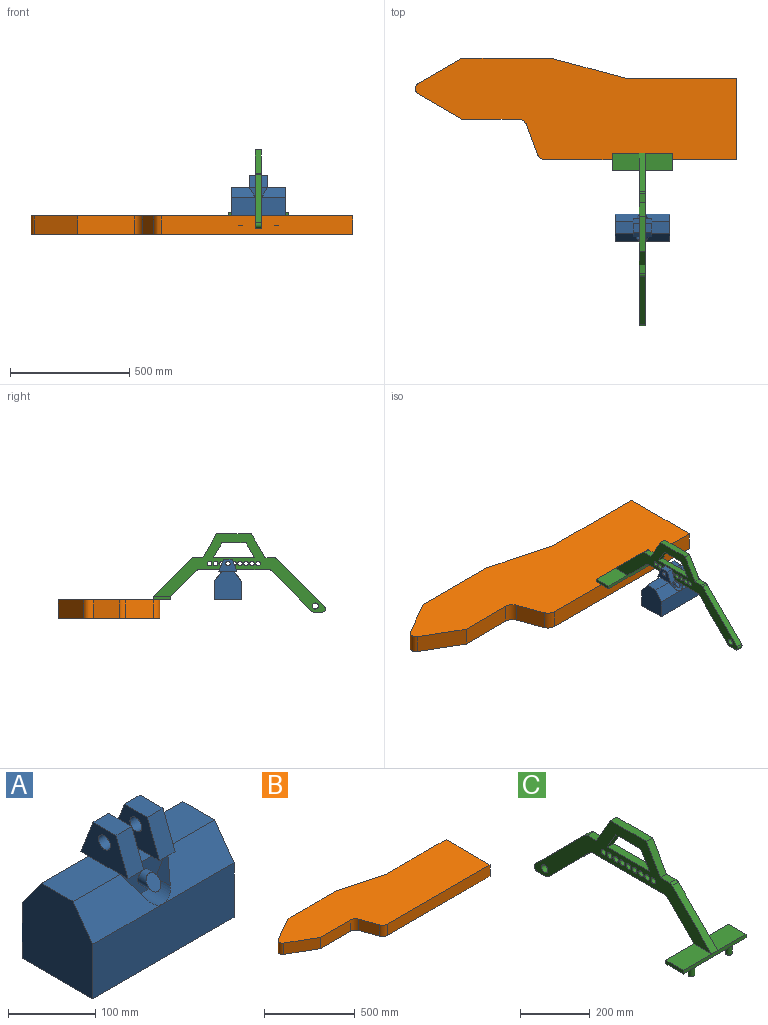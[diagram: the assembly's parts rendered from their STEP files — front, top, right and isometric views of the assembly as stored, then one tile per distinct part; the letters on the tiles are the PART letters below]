
ASSEMBLY  parts=3 mates=3
PART A: 40 faces, bbox 228.6x114.3x171.5 mm
  f0: plane 114.3x44.45mm, normal (0,0.81,0.58), area 4882.5mm2, adj f5,f6,f13,f35,f36
  f1: plane 114.3x44.45mm, normal (0,0.81,0.58), area 4882.5mm2, adj f4,f8,f13,f34,f35
  f2: plane 114.3x44.45mm, normal (0,-0.81,0.58), area 4882.5mm2, adj f4,f8,f14,f28,f31
  f3: plane 114.3x44.45mm, normal (0,-0.81,0.58), area 4882.5mm2, adj f5,f6,f14,f29,f31
  f4: plane 120.65x114.3mm, normal (1,0,0), area 12379mm2, adj f1,f2,f8,f13,f14,f15
  f5: plane 120.65x114.3mm, normal (-1,0,0), area 12379mm2, adj f0,f3,f6,f13,f14,f15
  f6: plane 76.2x50.8mm, normal (0,0,1), area 3871mm2, adj f0,f3,f5,f20
  f7: plane 50.8x25.4mm, normal (0,0,1), area 1290.3mm2, adj f22,f23,f32,f38
  f8: plane 76.2x50.8mm, normal (0,0,1), area 3871mm2, adj f1,f2,f4,f21
  f9: plane 37.2x25.4mm, normal (0,0,1), area 944.9mm2, adj f10,f12,f21,f22
  f10: plane 50.8x25.4mm, normal (0,0.93,0.36), area 1382.1mm2, adj f9,f21,f22,f27
  f11: cylinder r=9.53mm len=25.4mm, axis (1,0,0), area 1520.1mm2, adj f21,f22
  f12: plane 50.8x25.4mm, normal (0,-0.93,0.36), area 1382.1mm2, adj f9,f21,f22,f25
  f13: plane 228.6x76.2mm, normal (0,1,0), area 17419.3mm2, adj f0,f1,f4,f5,f15
  f14: plane 228.6x76.2mm, normal (0,-1,0), area 17419.3mm2, adj f2,f3,f4,f5,f15
  f15: plane 228.6x114.3mm, normal (0,0,-1), area 26129mm2, adj f4,f5,f13,f14
  f16: plane 37.2x25.4mm, normal (0,0,1), area 944.9mm2, adj f17,f19,f20,f23
  f17: plane 50.8x25.4mm, normal (0,0.93,0.36), area 1382.1mm2, adj f16,f20,f23,f26
  f18: cylinder r=9.53mm len=25.4mm, axis (1,0,0), area 1520.1mm2, adj f20,f23
  f19: plane 50.8x25.4mm, normal (0,-0.93,0.36), area 1382.1mm2, adj f16,f20,f23,f24
  f20: plane 76.2x50.8mm, normal (-1,0,0), area 2595.3mm2, adj f6,f16,f17,f18,f19,f24,f26
  f21: plane 76.2x50.8mm, normal (1,0,0), area 2595.3mm2, adj f8,f9,f10,f11,f12,f25,f27
  f22: plane 76.2x50.8mm, normal (-1,0,0), area 2595.3mm2, adj f7,f9,f10,f11,f12,f25,f27
  f23: plane 76.2x50.8mm, normal (1,0,0), area 2595.3mm2, adj f7,f16,f17,f18,f19,f24,f26
  f24: plane 25.4x12.7mm, normal (0,0,-1), area 322.6mm2, adj f19,f20,f23,f32
  f25: plane 25.4x12.7mm, normal (0,0,-1), area 322.6mm2, adj f12,f21,f22,f32
  f26: plane 25.4x12.7mm, normal (0,0,-1), area 322.6mm2, adj f17,f20,f23,f38
  f27: plane 25.4x12.7mm, normal (0,0,-1), area 322.6mm2, adj f10,f21,f22,f38
  f28: plane 33.17x23.69mm, normal (-0.87,0,0.49), area 451.3mm2, adj f2,f31,f32
  f29: plane 33.17x23.69mm, normal (0.87,0,0.49), area 451.3mm2, adj f3,f31,f32
  f30: cylinder r=9.53mm len=22.68mm, axis (0,-1,0), area 950.1mm2, adj f32,f33
  f31: cylinder r=22.23mm len=38.69mm, axis (0,-1,0), area 1359.5mm2, adj f2,f3,f28,f29,f32
  f32: plane 76.2x44.45mm, normal (0,-1,0), area 1930.2mm2, adj f7,f24,f25,f28,f29,f30,f31
  f33: plane 19.05x19.05mm, normal (0,-0.81,0.58), area 350.3mm2, adj f30
  f34: plane 33.17x23.69mm, normal (-0.87,0,0.49), area 451.3mm2, adj f1,f35,f38
  f35: cylinder r=22.23mm len=38.69mm, axis (0,1,0), area 1359.5mm2, adj f0,f1,f34,f36,f38
  f36: plane 33.17x23.69mm, normal (0.87,0,0.49), area 451.3mm2, adj f0,f35,f38
  f37: cylinder r=9.53mm len=22.68mm, axis (0,1,0), area 950.1mm2, adj f38,f39
  f38: plane 76.2x44.45mm, normal (0,1,0), area 1930.2mm2, adj f7,f26,f27,f34,f35,f36,f37
  f39: plane 19.05x19.05mm, normal (0,0.81,0.58), area 350.3mm2, adj f37
PART B: 14 faces, bbox 1346.2x425.5x76.2 mm
  f0: plane 376.93x76.2mm, normal (0,1,0), area 28722mm2, adj f1,f11,f12,f13
  f1: plane 181.87x105mm, normal (-0.5,0.87,0), area 16002.5mm2, adj f0,f2,f12,f13
  f2: cylinder r=25.4mm len=76.2mm, axis (0,0,-1), area 4053.7mm2, adj f1,f3,f12,f13
  f3: plane 181.87x105mm, normal (-0.5,-0.87,0), area 16002.5mm2, adj f2,f4,f12,f13
  f4: plane 235.95x76.2mm, normal (0,-1,0), area 17979.5mm2, adj f3,f5,f12,f13
  f5: cylinder r=38.1mm len=76.2mm, axis (0,0,-1), area 3547mm2, adj f4,f6,f12,f13
  f6: plane 121.31x76.2mm, normal (-0.94,-0.34,0), area 9837.2mm2, adj f5,f7,f12,f13
  f7: cylinder r=38.1mm len=76.2mm, axis (0,0,-1), area 3547mm2, adj f6,f8,f12,f13
  f8: plane 799.92x76.2mm, normal (0,-1,0), area 60953.9mm2, adj f7,f9,f12,f13
  f9: plane 342.9x76.2mm, normal (1,0,0), area 26129mm2, adj f8,f10,f12,f13
  f10: plane 466.62x76.2mm, normal (0,1,0), area 35556.4mm2, adj f9,f11,f12,f13
  f11: plane 308.08x82.55mm, normal (0.26,0.97,0), area 24303.9mm2, adj f0,f10,f12,f13
  f12: plane 1346.2x425.45mm, normal (0,0,1), area 415842.4mm2, adj f0,f1,f2,f3,f4,f5,f6,f7
  f13: plane 1346.2x425.45mm, normal (0,0,-1), area 415842.4mm2, adj f0,f1,f2,f3,f4,f5,f6,f7
PART C: 44 faces, bbox 254x722.6x327.8 mm
  f0: plane 203.2x203.2mm, normal (0,0.71,0.71), area 7299.2mm2, adj f1,f30,f31,f32
  f1: cylinder r=12.7mm len=25.4mm, axis (-1,0,0), area 253.4mm2, adj f0,f2,f31,f32
  f2: plane 38.1x25.4mm, normal (0,0,1), area 967.7mm2, adj f1,f3,f31,f32
  f3: plane 99.22x57.28mm, normal (0,0.87,0.5), area 2910.1mm2, adj f2,f4,f31,f32
  f4: plane 145.59x25.4mm, normal (0,0,1), area 3698.1mm2, adj f3,f5,f31,f32
  f5: plane 99.22x57.28mm, normal (0,-0.87,0.5), area 2910.1mm2, adj f4,f6,f31,f32
  f6: plane 38.1x25.4mm, normal (0,0,1), area 967.7mm2, adj f5,f7,f31,f32
  f7: cylinder r=12.7mm len=25.4mm, axis (-1,0,0), area 253.4mm2, adj f6,f8,f31,f32
  f8: plane 161.38x161.38mm, normal (0,-0.71,0.71), area 5796.9mm2, adj f7,f31,f32,f34
  f9: plane 110.58x110.58mm, normal (0,0.71,-0.71), area 3972.2mm2, adj f10,f31,f32,f36
  f10: cylinder r=12.7mm len=25.4mm, axis (-1,0,0), area 253.4mm2, adj f9,f11,f31,f32
  f11: plane 294.28x25.4mm, normal (0,0,-1), area 7474.7mm2, adj f10,f12,f31,f32
  f12: cylinder r=12.7mm len=25.4mm, axis (-1,0,0), area 253.4mm2, adj f11,f13,f31,f32
  f13: plane 170.36x170.36mm, normal (0,-0.71,-0.71), area 6119.5mm2, adj f12,f14,f31,f32
  f14: cylinder r=12.7mm len=25.4mm, axis (-1,0,0), area 253.4mm2, adj f13,f15,f31,f32
  f15: plane 35.92x25.4mm, normal (0,0,-1), area 912.4mm2, adj f14,f30,f31,f32
  f16: plane 172.18x25.4mm, normal (0,0,1), area 4373.2mm2, adj f17,f19,f31,f32
  f17: plane 61.12x35.29mm, normal (0,0.87,-0.5), area 1792.6mm2, adj f16,f18,f31,f32
  f18: plane 101.6x25.4mm, normal (0,0,-1), area 2580.6mm2, adj f17,f19,f31,f32
  f19: plane 61.12x35.29mm, normal (0,-0.87,-0.5), area 1792.6mm2, adj f16,f18,f31,f32
  f20: cylinder r=9.53mm len=25.4mm, axis (-1,0,0), area 1520.1mm2, adj f31,f32
  f21: cylinder r=9.53mm len=25.4mm, axis (-1,0,0), area 1520.1mm2, adj f31,f32
  f22: cylinder r=9.53mm len=25.4mm, axis (-1,0,0), area 1520.1mm2, adj f31,f32
  f23: cylinder r=9.53mm len=25.4mm, axis (-1,0,0), area 1520.1mm2, adj f31,f32
  f24: cylinder r=9.53mm len=25.4mm, axis (-1,0,0), area 1520.1mm2, adj f31,f32
  f25: cylinder r=9.53mm len=25.4mm, axis (-1,0,0), area 1520.1mm2, adj f31,f32
  f26: cylinder r=9.53mm len=25.4mm, axis (-1,0,0), area 1520.1mm2, adj f31,f32
  f27: cylinder r=9.53mm len=25.4mm, axis (-1,0,0), area 1520.1mm2, adj f31,f32
  f28: cylinder r=9.53mm len=25.4mm, axis (-1,0,0), area 1520.1mm2, adj f31,f32
  f29: cylinder r=12.7mm len=25.4mm, axis (-1,0,0), area 2026.8mm2, adj f31,f32
  f30: cylinder r=12.7mm len=25.4mm, axis (-1,0,0), area 760.1mm2, adj f0,f15,f31,f32
  f31: plane 722.62x327.82mm, normal (1,0,0), area 49675.7mm2, adj f0,f1,f2,f3,f4,f5,f6,f7
  f32: plane 722.62x327.82mm, normal (-1,0,0), area 49675.7mm2, adj f0,f1,f2,f3,f4,f5,f6,f7
  f33: plane 114.3x71.84mm, normal (0,0,1), area 8211.5mm2, adj f32,f34,f36,f37
  f34: plane 254x12.7mm, normal (0,-1,0), area 3225.8mm2, adj f8,f33,f35,f37,f38,f39
  f35: plane 71.84x12.7mm, normal (1,0,0), area 912.4mm2, adj f34,f36,f38,f39
  f36: plane 254x12.7mm, normal (0,1,0), area 3225.8mm2, adj f9,f33,f35,f37,f38,f39
  f37: plane 71.84x12.7mm, normal (-1,0,0), area 912.4mm2, adj f33,f34,f36,f38
  f38: plane 254x71.84mm, normal (0,0,-1), area 17677.8mm2, adj f34,f35,f36,f37,f40,f42
  f39: plane 114.3x71.84mm, normal (0,0,1), area 8211.5mm2, adj f31,f34,f35,f36
  f40: cylinder r=9.53mm len=38.1mm, axis (0,0,1), area 2280.2mm2, adj f38,f41
  f41: plane 19.05x19.05mm, normal (0,0,-1), area 285mm2, adj f40
  f42: cylinder r=9.53mm len=38.1mm, axis (0,0,1), area 2280.2mm2, adj f38,f43
  f43: plane 19.05x19.05mm, normal (0,0,-1), area 285mm2, adj f42
PLACE A rot(axis=(0,0,1),180deg) t=(-509.11,-227.42,76.2)mm
PLACE B at identity fixed
PLACE C rot(axis=(0,0,1),180deg) t=(-394.81,-43.27,88.9)mm
MATE planar B.f12 <-> C.f38  axis (0,0,1) through (-598.65,212.65,76.2)mm
MATE cylindrical A.f11 <-> C.f23  axis (-1,0,0) through (-432.91,-284.57,228.6)mm
MATE planar A.f23 <-> C.f32  axis (-1,0,0) through (-382.11,-284.57,218.32)mm
